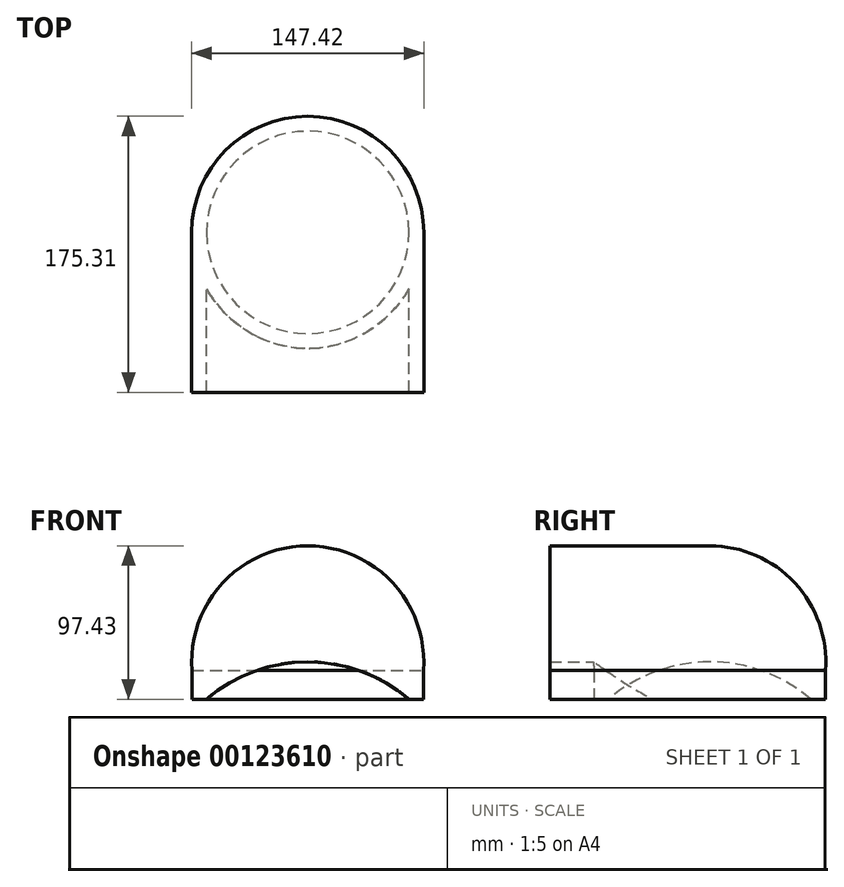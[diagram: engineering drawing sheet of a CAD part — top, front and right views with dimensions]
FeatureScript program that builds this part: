
annotation { "Feature Type Name" : "Feature", "Feature Type Description" : "" }
export const myFeature = defineFeature(function(context is Context, id is Id, definition is map)
    precondition{}
    {
        {
            var Q0;
            Q0=qCreatedBy(makeId("Front.planeOp"),FACE);
            var sketch = newSketch(context, id + "F0", { "sketchPlane" : qUnion([Q0])});
            skArc(sketch, "E0", {"start": v(64.25, 0) * mm, "mid": v(0, 23.72) * mm, "end": v(-64.25, 0) * mm});
            skLineSegment(sketch, "E1", {"start": v(-73.5, 0) * mm, "end": v(-64.25, 0) * mm});
            skLineSegment(sketch, "E2.trimOffspring", {"start": v(64.25, 0) * mm, "end": v(73.5, 0) * mm});
            skLineSegment(sketch, "E3", {"start": v(-73.5, 0) * mm, "end": v(-73.5, 29.15) * mm});
            skLineSegment(sketch, "E4", {"start": v(73.5, 0) * mm, "end": v(73.5, 29.15) * mm});
            skArc(sketch, "E5", {"start": v(73.5, 18.3) * mm, "mid": v(0, 97.43) * mm, "end": v(-73.5, 18.3) * mm});
            skSolve(sketch);
        }
        {
            var Q0;
            Q0 = qSketchRegion(id + "F0", true);
            extrude(context, id + "F1", {"entities" : qUnion([Q0]), "depth" : 101.6 * mm});
        }
        {
            var Q0;
            Q0=makeQuery(id+"F1.opExtrude","CAP_FACE",FACE,{"disambiguationData":[OSD([sQuery(id+"F0.wireOp",EDGE,"E0"),sQuery(id+"F0.wireOp",EDGE,"E1"),sQuery(id+"F0.wireOp",EDGE,"E2.trimOffspring"),sQuery(id+"F0.wireOp",EDGE,"E3"),sQuery(id+"F0.wireOp",EDGE,"E4"),sQuery(id+"F0.wireOp",EDGE,"E5")])],"isStart":true});
            var sketch = newSketch(context, id + "F2", { "sketchPlane" : qUnion([Q0])});
            skLineSegment(sketch, "E6", {"start": v(0, 23.72) * mm, "end": v(0, 97.43) * mm});
            skSolve(sketch);
        }
        {
            var Q0;
            Q0 = qSketchRegion(id + "F2", true);
            var Q1;
            {var subQ2=sQuery(id+"F2.wireOp",EDGE,"E6");Q1=makeQuery(id+"F2.imprint","IMPRINT",FACE,{"disambiguationData":[TD([[makeQuery(id+"F2.imprint","IMPRINT",EDGE,{"derivedFrom":subQ2}),-1.0]])]});}
            var Q2;
            Q2=sQuery(id+"F2.wireOp",EDGE,"E6");
            revolve(context, id + "F3", {"operationType" : NewBodyOperationType.ADD, "entities" : qUnion([Q0, Q1]), "axis" : qUnion([Q2]), "revolveType" : RevolveType.FULL});
        }
    });
